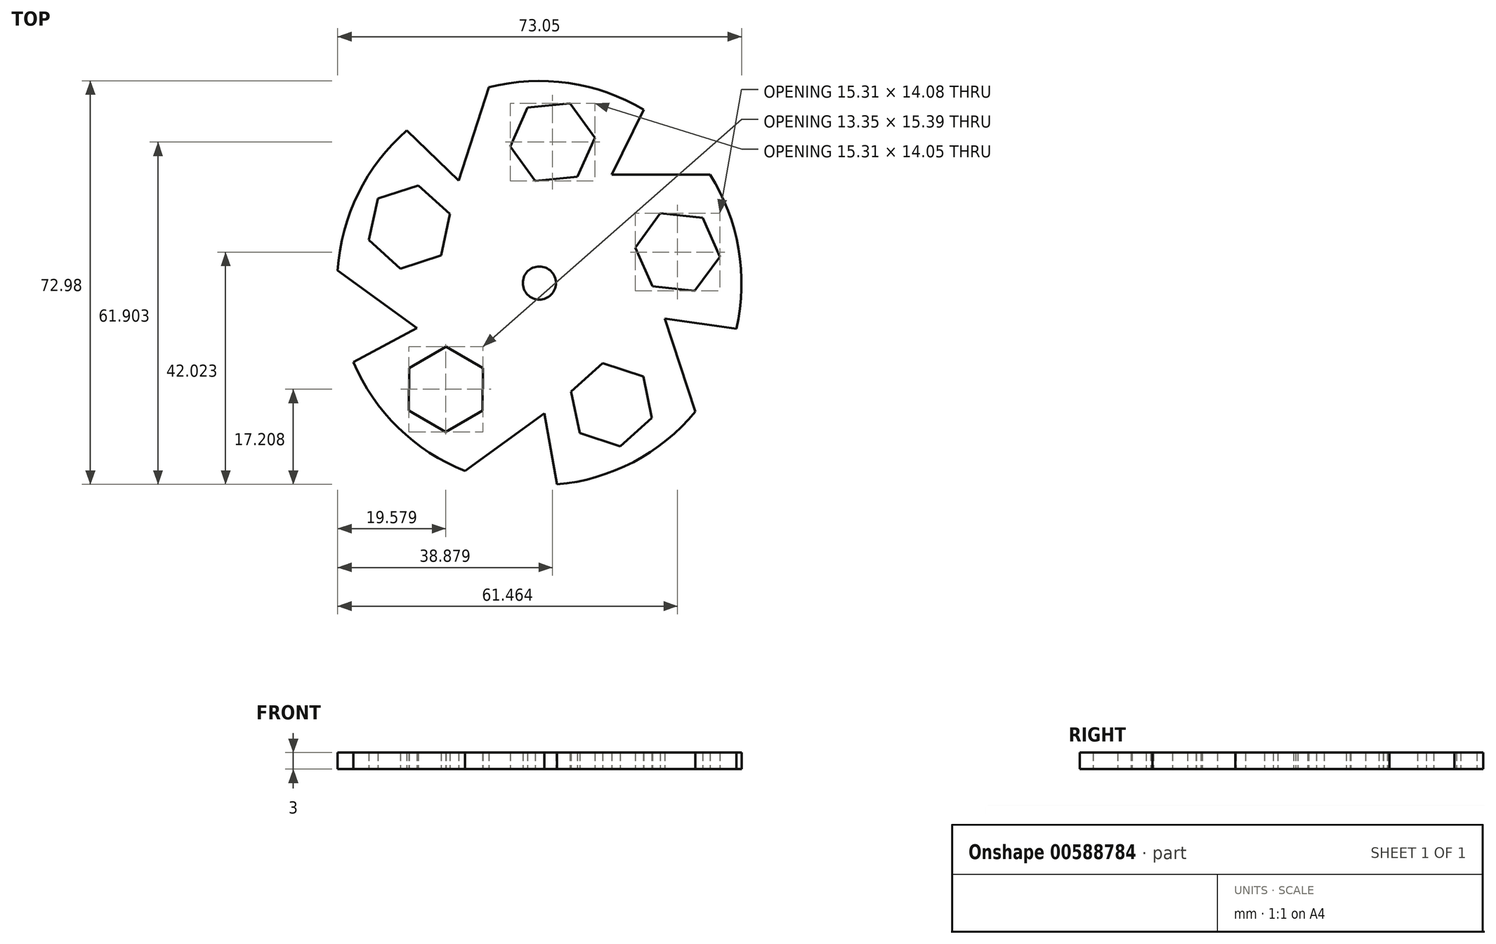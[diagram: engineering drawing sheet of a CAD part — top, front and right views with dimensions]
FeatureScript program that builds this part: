
annotation { "Feature Type Name" : "Feature", "Feature Type Description" : "" }
export const myFeature = defineFeature(function(context is Context, id is Id, definition is map)
    precondition{}
    {
        {
            var Q0;
            Q0=qCreatedBy(makeId("Top.planeOp"),FACE);
            var sketch = newSketch(context, id + "F0", { "sketchPlane" : qUnion([Q0])});
            skLineSegment(sketch, "E0.bottom", {"start": v(-37.7, 36.8) * mm, "end": v(37.3, 36.8) * mm});
            skLineSegment(sketch, "E0.top", {"start": v(-37.7, -38.2) * mm, "end": v(37.3, -38.2) * mm});
            skLineSegment(sketch, "E0.left", {"start": v(-37.7, 36.8) * mm, "end": v(-37.7, -38.2) * mm});
            skLineSegment(sketch, "E0.right", {"start": v(37.3, 36.8) * mm, "end": v(37.3, -38.2) * mm});
            skCircle(sketch, "E1", {"center": v(0, 0) * mm, "radius": 36.56 * mm});
            skLineSegment(sketch, "E2.0", {"start": v(10.05, 26.27) * mm, "end": v(6.9, 19.25) * mm});
            skLineSegment(sketch, "E2.1", {"start": v(6.9, 19.25) * mm, "end": v(-0.76, 18.46) * mm});
            skLineSegment(sketch, "E2.2", {"start": v(-0.76, 18.46) * mm, "end": v(-5.27, 24.7) * mm});
            skLineSegment(sketch, "E2.3", {"start": v(-5.27, 24.7) * mm, "end": v(-2.12, 31.72) * mm});
            skLineSegment(sketch, "E2.4", {"start": v(-2.12, 31.72) * mm, "end": v(5.54, 32.5) * mm});
            skLineSegment(sketch, "E2.5", {"start": v(5.54, 32.5) * mm, "end": v(10.05, 26.27) * mm});
            skPoint(sketch, "E2.0.midPoint", {"position": v(8.47, 22.76) * mm});
            skLineSegment(sketch, "E3.1.0", {"start": v(-17.79, 4.98) * mm, "end": v(-25.12, 2.62) * mm});
            skLineSegment(sketch, "E3.1.2", {"start": v(-30.82, 7.79) * mm, "end": v(-29.2, 15.31) * mm});
            skLineSegment(sketch, "E3.1.3", {"start": v(-29.2, 15.31) * mm, "end": v(-21.88, 17.67) * mm});
            skLineSegment(sketch, "E3.1.4", {"start": v(-21.88, 17.67) * mm, "end": v(-16.17, 12.5) * mm});
            skLineSegment(sketch, "E3.1.5", {"start": v(-16.17, 12.5) * mm, "end": v(-17.79, 4.98) * mm});
            skLineSegment(sketch, "E3.1.6", {"start": v(-25.12, 2.62) * mm, "end": v(-30.82, 7.79) * mm});
            skLineSegment(sketch, "E3.2.0", {"start": v(-10.24, -15.38) * mm, "end": v(-10.25, -23.08) * mm});
            skLineSegment(sketch, "E3.2.2", {"start": v(-16.93, -26.9) * mm, "end": v(-23.59, -23.04) * mm});
            skLineSegment(sketch, "E3.2.3", {"start": v(-23.59, -23.04) * mm, "end": v(-23.57, -15.35) * mm});
            skLineSegment(sketch, "E3.2.4", {"start": v(-23.57, -15.35) * mm, "end": v(-16.9, -11.52) * mm});
            skLineSegment(sketch, "E3.2.5", {"start": v(-16.9, -11.52) * mm, "end": v(-10.24, -15.38) * mm});
            skLineSegment(sketch, "E3.2.6", {"start": v(-10.25, -23.08) * mm, "end": v(-16.93, -26.9) * mm});
            skLineSegment(sketch, "E4.1.3.0", {"start": v(11.46, -14.49) * mm, "end": v(18.78, -16.88) * mm});
            skLineSegment(sketch, "E4.5.3.0", {"start": v(20.36, -24.42) * mm, "end": v(14.63, -29.55) * mm});
            skLineSegment(sketch, "E4.8.3.0", {"start": v(14.63, -29.55) * mm, "end": v(7.31, -27.16) * mm});
            skLineSegment(sketch, "E4.11.3.0", {"start": v(7.31, -27.16) * mm, "end": v(5.73, -19.62) * mm});
            skLineSegment(sketch, "E4.14.3.0", {"start": v(5.73, -19.62) * mm, "end": v(11.46, -14.49) * mm});
            skLineSegment(sketch, "E4.17.3.0", {"start": v(18.78, -16.88) * mm, "end": v(20.36, -24.42) * mm});
            skLineSegment(sketch, "E4.1.4.0", {"start": v(17.32, 6.42) * mm, "end": v(21.86, 12.64) * mm});
            skLineSegment(sketch, "E4.5.4.0", {"start": v(29.51, 11.82) * mm, "end": v(32.63, 4.78) * mm});
            skLineSegment(sketch, "E4.8.4.0", {"start": v(32.63, 4.78) * mm, "end": v(28.09, -1.44) * mm});
            skLineSegment(sketch, "E4.11.4.0", {"start": v(28.09, -1.44) * mm, "end": v(20.44, -0.61) * mm});
            skLineSegment(sketch, "E4.14.4.0", {"start": v(20.44, -0.61) * mm, "end": v(17.32, 6.42) * mm});
            skLineSegment(sketch, "E4.17.4.0", {"start": v(21.86, 12.64) * mm, "end": v(29.51, 11.82) * mm});
            skLineSegment(sketch, "E5", {"start": v(18.85, 31.33) * mm, "end": v(13.1, 19.61) * mm});
            skLineSegment(sketch, "E6", {"start": v(13.1, 19.61) * mm, "end": v(30.86, 19.61) * mm});
            skLineSegment(sketch, "E7.1.0", {"start": v(-23.97, 27.6) * mm, "end": v(-14.6, 18.52) * mm});
            skLineSegment(sketch, "E7.1.1", {"start": v(-14.6, 18.52) * mm, "end": v(-9.12, 35.4) * mm});
            skLineSegment(sketch, "E7.2.0", {"start": v(-33.66, -14.27) * mm, "end": v(-22.13, -8.17) * mm});
            skLineSegment(sketch, "E7.2.1", {"start": v(-22.13, -8.17) * mm, "end": v(-36.5, 2.27) * mm});
            skLineSegment(sketch, "E7.3.0", {"start": v(3.17, -36.42) * mm, "end": v(0.93, -23.57) * mm});
            skLineSegment(sketch, "E7.3.1", {"start": v(0.93, -23.57) * mm, "end": v(-13.43, -34) * mm});
            skLineSegment(sketch, "E7.4.0", {"start": v(35.62, -8.24) * mm, "end": v(22.7, -6.4) * mm});
            skLineSegment(sketch, "E7.4.1", {"start": v(22.7, -6.4) * mm, "end": v(28.19, -23.29) * mm});
            skCircle(sketch, "E8", {"center": v(0, 0) * mm, "radius": 3 * mm});
            skSolve(sketch);
        }
        {
            var Q0;
            Q0=makeQuery(id+"F0.imprint","IMPRINT",FACE,{"disambiguationData":[TD([[makeQuery(id+"F0.imprint","IMPRINT",EDGE,{"derivedFrom":sQuery(id+"F0.wireOp",EDGE,"E2.0")}),1.0]])]});
            extrude(context, id + "F1", {"entities" : qUnion([Q0]), "depth" : 3 * mm, "offsetDistance" : 25 * mm});
        }
    });
